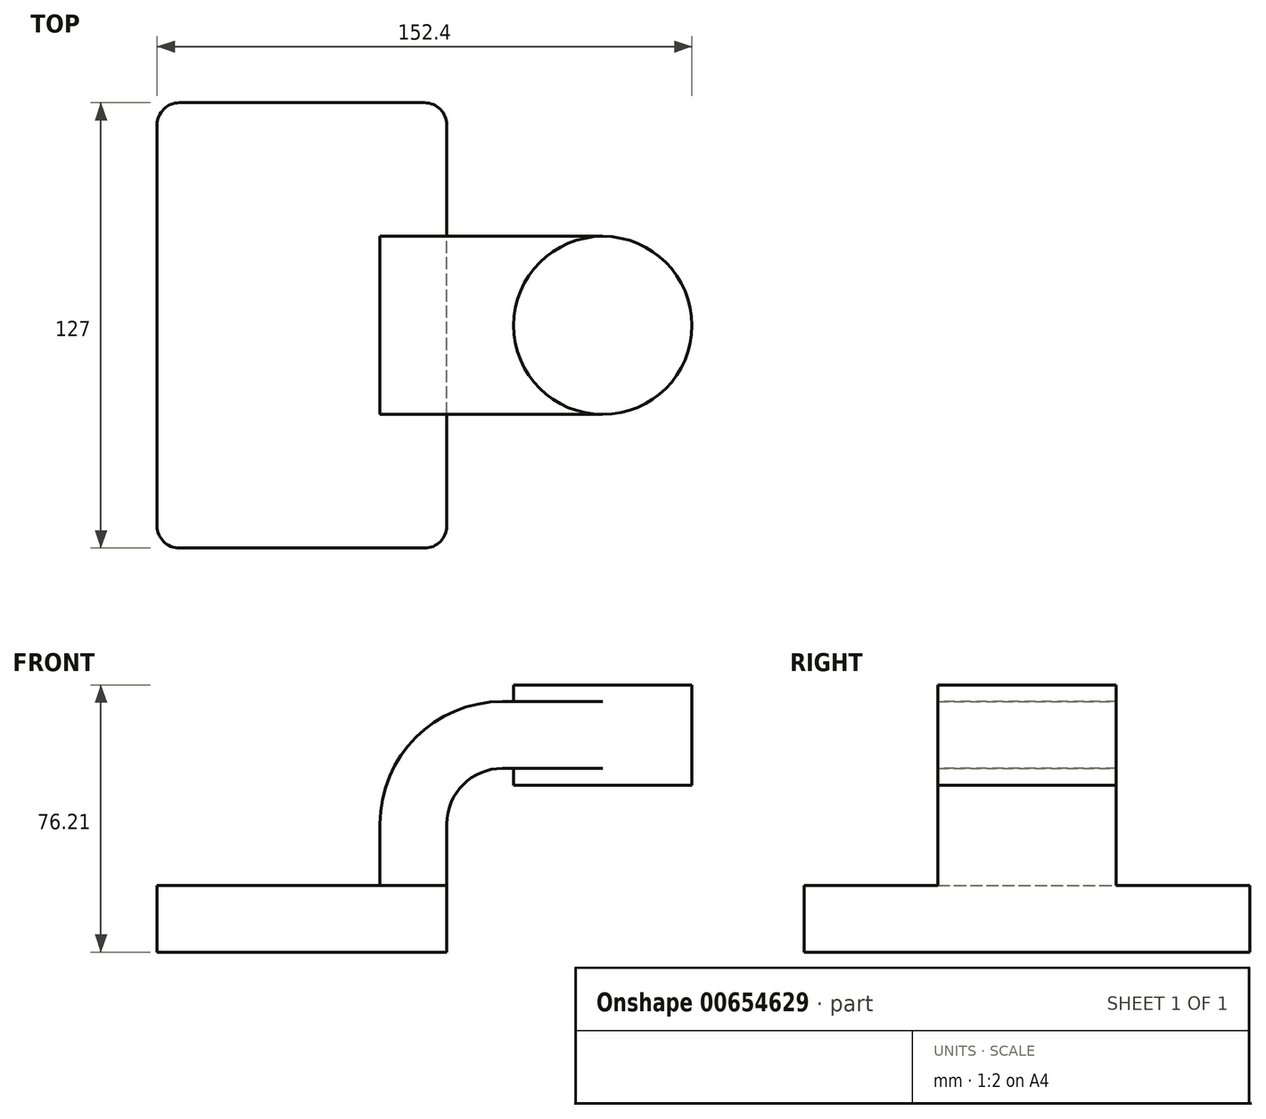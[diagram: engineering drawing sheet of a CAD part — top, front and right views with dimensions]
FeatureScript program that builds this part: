
annotation { "Feature Type Name" : "Feature", "Feature Type Description" : "" }
export const myFeature = defineFeature(function(context is Context, id is Id, definition is map)
    precondition{}
    {
        {
            var Q0;
            Q0=qCreatedBy(makeId("Front.planeOp"),FACE);
            var sketch = newSketch(context, id + "F0", { "sketchPlane" : qUnion([Q0])});
            skLineSegment(sketch, "E0.bottom", {"start": v(41.28, -9.52) * mm, "end": v(-41.28, -9.53) * mm});
            skLineSegment(sketch, "E0.top", {"start": v(41.28, 9.53) * mm, "end": v(-41.28, 9.53) * mm});
            skLineSegment(sketch, "E0.left", {"start": v(41.28, -9.52) * mm, "end": v(41.28, 9.53) * mm});
            skLineSegment(sketch, "E0.right", {"start": v(-41.28, -9.52) * mm, "end": v(-41.28, 9.53) * mm});
            skPoint(sketch, "E0.middle", {"position": v(0, 0) * mm});
            skLineSegment(sketch, "E1.bottom", {"start": v(111.12, 38.1) * mm, "end": v(60.32, 38.1) * mm});
            skLineSegment(sketch, "E1.top", {"start": v(111.12, 66.68) * mm, "end": v(60.32, 66.68) * mm});
            skLineSegment(sketch, "E1.left", {"start": v(111.12, 38.1) * mm, "end": v(111.12, 66.68) * mm});
            skLineSegment(sketch, "E1.right", {"start": v(60.32, 38.1) * mm, "end": v(60.32, 66.68) * mm});
            skPoint(sketch, "E1.middle", {"position": v(85.72, 52.39) * mm});
            skLineSegment(sketch, "E2", {"start": v(41.28, 9.53) * mm, "end": v(41.28, 27) * mm});
            skArc(sketch, "E3", {"start": v(41.27, 27) * mm, "mid": v(45.92, 38.23) * mm, "end": v(57.15, 42.88) * mm});
            skLineSegment(sketch, "E4", {"start": v(57.15, 42.88) * mm, "end": v(85.72, 42.88) * mm});
            skLineSegment(sketch, "E5.0", {"start": v(57.15, 61.93) * mm, "end": v(85.82, 61.93) * mm});
            skArc(sketch, "E5.1", {"start": v(22.23, 27) * mm, "mid": v(32.45, 51.7) * mm, "end": v(57.15, 61.93) * mm});
            skLineSegment(sketch, "E5.2", {"start": v(22.22, 9.53) * mm, "end": v(22.22, 27) * mm});
            skFitSpline(sketch, "E6", {"points": [v(-41.28, 9.52) * mm, v(57.15, 61.93) * mm], "startDerivative": vector(53.13, 101.84) * mm, "endDerivative": vector(122.5, -1.13) * mm});
            skLineSegment(sketch, "E7", {"start": v(85.72, 66.68) * mm, "end": v(85.72, 38.1) * mm});
            skSolve(sketch);
        }
        {
            var Q0;
            Q0=makeQuery(id+"F0.imprint","IMPRINT",FACE,{"disambiguationData":[TD([[makeQuery(id+"F0.imprint","IMPRINT",EDGE,{"derivedFrom":sQuery(id+"F0.wireOp",EDGE,"E0.bottom")}),-1.0]])]});
            extrude(context, id + "F1", {"entities" : qUnion([Q0]), "endBound" : BoundingType.SYMMETRIC, "depth" : 127 * mm, "offsetDistance" : 25.4 * mm});
        }
        {
            var Q0;
            {var subQ0=sQuery(id+"F0.wireOp",EDGE,"E4");var subQ1=sQuery(id+"F0.wireOp",EDGE,"E1.right");var subQ2=makeQuery(id+"F0.imprint","INTERSECT",VERTEX,{"derivedFrom":[subQ1,subQ0]});Q0=makeQuery(id+"F0.imprint","IMPRINT",FACE,{"disambiguationData":[TD([[makeQuery(id+"F0.imprint","IMPRINT",EDGE,{"disambiguationData":[TD([[subQ2,-1.0]])],"derivedFrom":subQ1}),-1.0]])]});}
            var Q1;
            {var subQ1=sQuery(id+"F0.wireOp",EDGE,"E2");Q1=makeQuery(id+"F0.imprint","IMPRINT",FACE,{"disambiguationData":[TD([[makeQuery(id+"F0.imprint","IMPRINT",EDGE,{"derivedFrom":subQ1}),1.0]])]});}
            extrude(context, id + "F2", {"entities" : qUnion([Q0, Q1]), "operationType" : NewBodyOperationType.ADD, "endBound" : BoundingType.SYMMETRIC, "depth" : 50.8 * mm, "offsetDistance" : 25.4 * mm});
        }
        {
            var Q0;
            Q0=makeQuery(id+"F0.imprint","IMPRINT",FACE,{"disambiguationData":[TD([[makeQuery(id+"F0.imprint","IMPRINT",EDGE,{"derivedFrom":sQuery(id+"F0.wireOp",EDGE,"E5.1")}),1.0]])]});
            extrude(context, id + "F3", {"entities" : qUnion([Q0]), "operationType" : NewBodyOperationType.ADD, "endBound" : BoundingType.SYMMETRIC, "depth" : 15.88 * mm, "offsetDistance" : 25.4 * mm});
        }
        {
            var Q0;
            {var subQ0=sQuery(id+"F0.wireOp",EDGE,"E1.left");Q0=makeQuery(id+"F0.imprint","IMPRINT",FACE,{"disambiguationData":[TD([[makeQuery(id+"F0.imprint","IMPRINT",EDGE,{"derivedFrom":subQ0}),1.0]])]});}
            var Q1;
            Q1=sQuery(id+"F0.wireOp",EDGE,"E7");
            revolve(context, id + "F4", {"operationType" : NewBodyOperationType.ADD, "entities" : qUnion([Q0]), "axis" : qUnion([Q1]), "revolveType" : RevolveType.FULL});
        }
        {
            var Q0;
            Q0=makeQuery(id+"F1.opExtrude","CAP_EDGE",EDGE,{"disambiguationData":[OSD([sQuery(id+"F0.wireOp",EDGE,"E0.left")])],"isStart":false});
            var Q1;
            Q1=makeQuery(id+"F1.opExtrude","CAP_EDGE",EDGE,{"disambiguationData":[OSD([sQuery(id+"F0.wireOp",EDGE,"E0.right")])],"isStart":false});
            var Q2;
            Q2=makeQuery(id+"F1.opExtrude","CAP_EDGE",EDGE,{"disambiguationData":[OSD([sQuery(id+"F0.wireOp",EDGE,"E0.right")])],"isStart":true});
            var Q3;
            Q3=makeQuery(id+"F1.opExtrude","CAP_EDGE",EDGE,{"disambiguationData":[OSD([sQuery(id+"F0.wireOp",EDGE,"E0.left")])],"isStart":true});
            fillet(context, id + "F5", {"entities" : qUnion([Q0, Q1, Q2, Q3]), "radius" : 6.35 * mm, "tangentPropagation" : true, "allowEdgeOverflow" : false});
        }
    });
